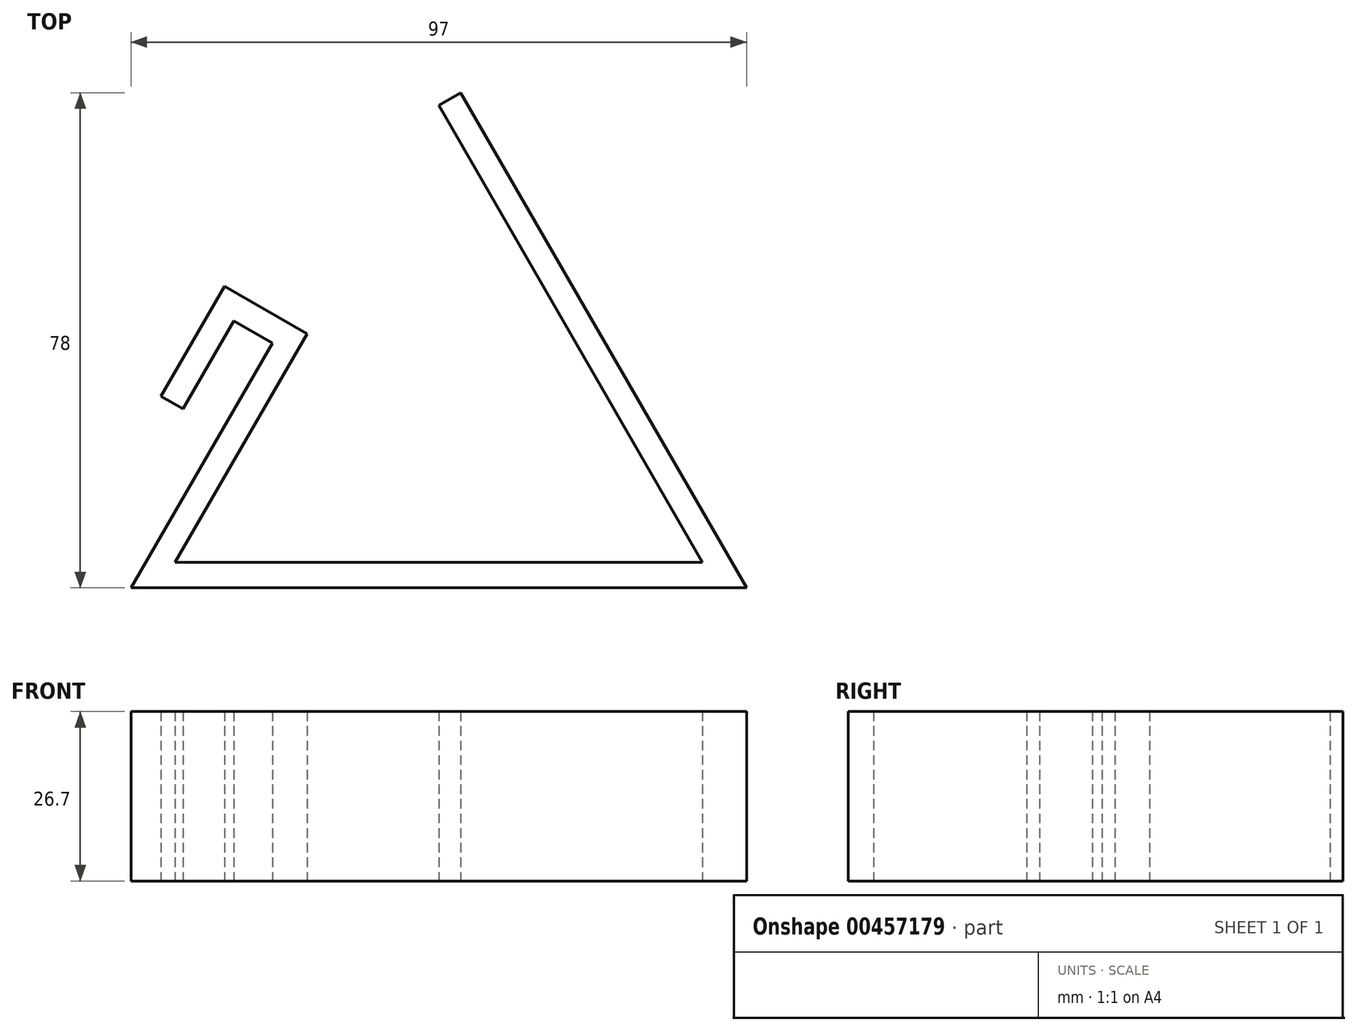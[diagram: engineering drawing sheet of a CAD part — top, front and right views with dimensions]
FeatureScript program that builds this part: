
annotation { "Feature Type Name" : "Feature", "Feature Type Description" : "" }
export const myFeature = defineFeature(function(context is Context, id is Id, definition is map)
    precondition{}
    {
        {
            var Q0;
            Q0=qCreatedBy(makeId("Top.planeOp"),FACE);
            var sketch = newSketch(context, id + "F0", { "sketchPlane" : qUnion([Q0])});
            skCircle(sketch, "E0.cCircle", {"center": v(0, 0) * mm, "radius": 24 * mm, "construction": true});
            skLineSegment(sketch, "E0.0", {"start": v(41.57, -24) * mm, "end": v(-41.57, -24) * mm});
            skLineSegment(sketch, "E0.1", {"start": v(-41.57, -24) * mm, "end": v(-20.78, 12) * mm});
            skLineSegment(sketch, "E0.2", {"start": v(0, 48) * mm, "end": v(41.57, -24) * mm});
            skPoint(sketch, "E0.0.midPoint", {"position": v(0, -24) * mm});
            skLineSegment(sketch, "E1", {"start": v(-20.78, 12) * mm, "end": v(-33.77, 19.5) * mm});
            skLineSegment(sketch, "E2", {"start": v(-33.77, 19.5) * mm, "end": v(-43.77, 2.18) * mm});
            skLineSegment(sketch, "E3.0", {"start": v(-32.31, 14.04) * mm, "end": v(-40.31, 0.18) * mm});
            skLineSegment(sketch, "E3.1", {"start": v(3.46, 50) * mm, "end": v(48.5, -28) * mm});
            skLineSegment(sketch, "E3.2", {"start": v(48.5, -28) * mm, "end": v(-48.5, -28) * mm});
            skLineSegment(sketch, "E3.3", {"start": v(-48.5, -28) * mm, "end": v(-26.25, 10.54) * mm});
            skLineSegment(sketch, "E3.4", {"start": v(-26.25, 10.54) * mm, "end": v(-32.31, 14.04) * mm});
            skLineSegment(sketch, "E4", {"start": v(0, 48) * mm, "end": v(3.46, 50) * mm});
            skLineSegment(sketch, "E5", {"start": v(-43.77, 2.18) * mm, "end": v(-40.31, 0.18) * mm});
            skSolve(sketch);
        }
        {
            var Q0;
            Q0 = qSketchRegion(id + "F0", true);
            extrude(context, id + "F1", {"entities" : qUnion([Q0]), "depth" : 26.7 * mm});
        }
    });
